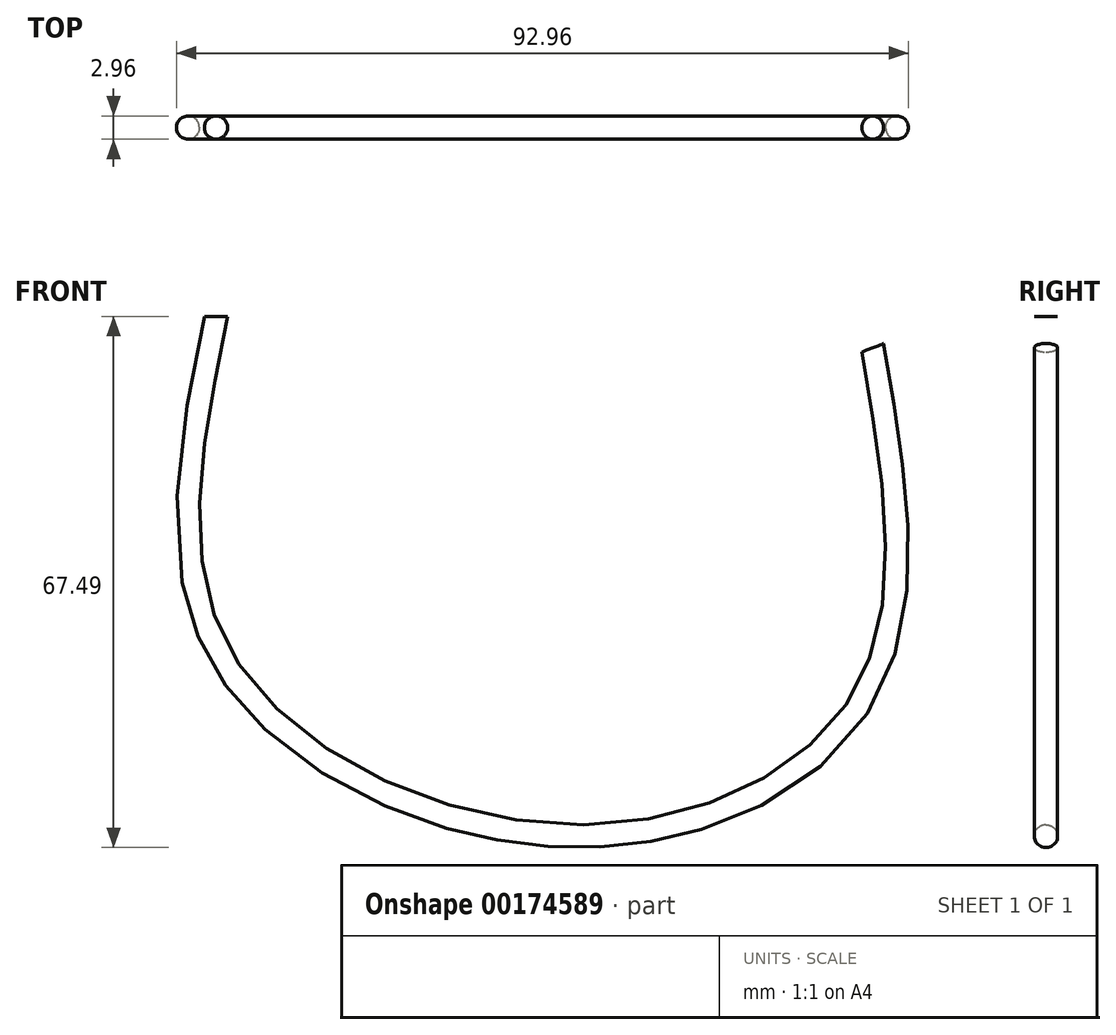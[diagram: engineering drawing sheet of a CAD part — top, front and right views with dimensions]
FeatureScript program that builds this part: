
annotation { "Feature Type Name" : "Feature", "Feature Type Description" : "" }
export const myFeature = defineFeature(function(context is Context, id is Id, definition is map)
    precondition{}
    {
        {
            var Q0;
            Q0=qCreatedBy(makeId("Front.planeOp"),FACE);
            var sketch = newSketch(context, id + "F0", { "sketchPlane" : qUnion([Q0])});
            skFitSpline(sketch, "E0", {"points": [v(-35.78, 26.25) * mm, v(-35.2, -16.57) * mm, v(8.8, -39.45) * mm, v(46.63, -21.56) * mm, v(47.51, 22.73) * mm], "startDerivative": vector(-38.35, -187.91) * mm, "endDerivative": vector(-34.1, 196.28) * mm});
            skSolve(sketch);
        }
        {
            var Q0;
            Q0=qCreatedBy(makeId("Top.planeOp"),FACE);
            cPlane(context, id + "F1", {"entities" : qUnion([Q0]), "cplaneType" : CPlaneType.OFFSET, "offset" : 26.5 * mm, "width" : 150 * mm, "height" : 150 * mm});
        }
        {
            var Q0;
            Q0=qCreatedBy(id+"F1.planeOp",FACE);
            var sketch = newSketch(context, id + "F2", { "sketchPlane" : qUnion([Q0])});
            skCircle(sketch, "E1", {"center": v(-35.8, 0) * mm, "radius": 1.48 * mm});
            skSolve(sketch);
        }
        {
            var Q0;
            Q0=makeQuery(id+"F2.imprint","IMPRINT",FACE,{"disambiguationData":[TD([[makeQuery(id+"F2.imprint","IMPRINT",EDGE,{"derivedFrom":sQuery(id+"F2.wireOp",EDGE,"E1")}),1.0]])]});
            var Q1;
            Q1=sQuery(id+"F0.wireOp",EDGE,"E0");
            sweep(context, id + "F3", {"profiles" : qUnion([Q0]), "path" : qUnion([Q1])});
        }
    });
